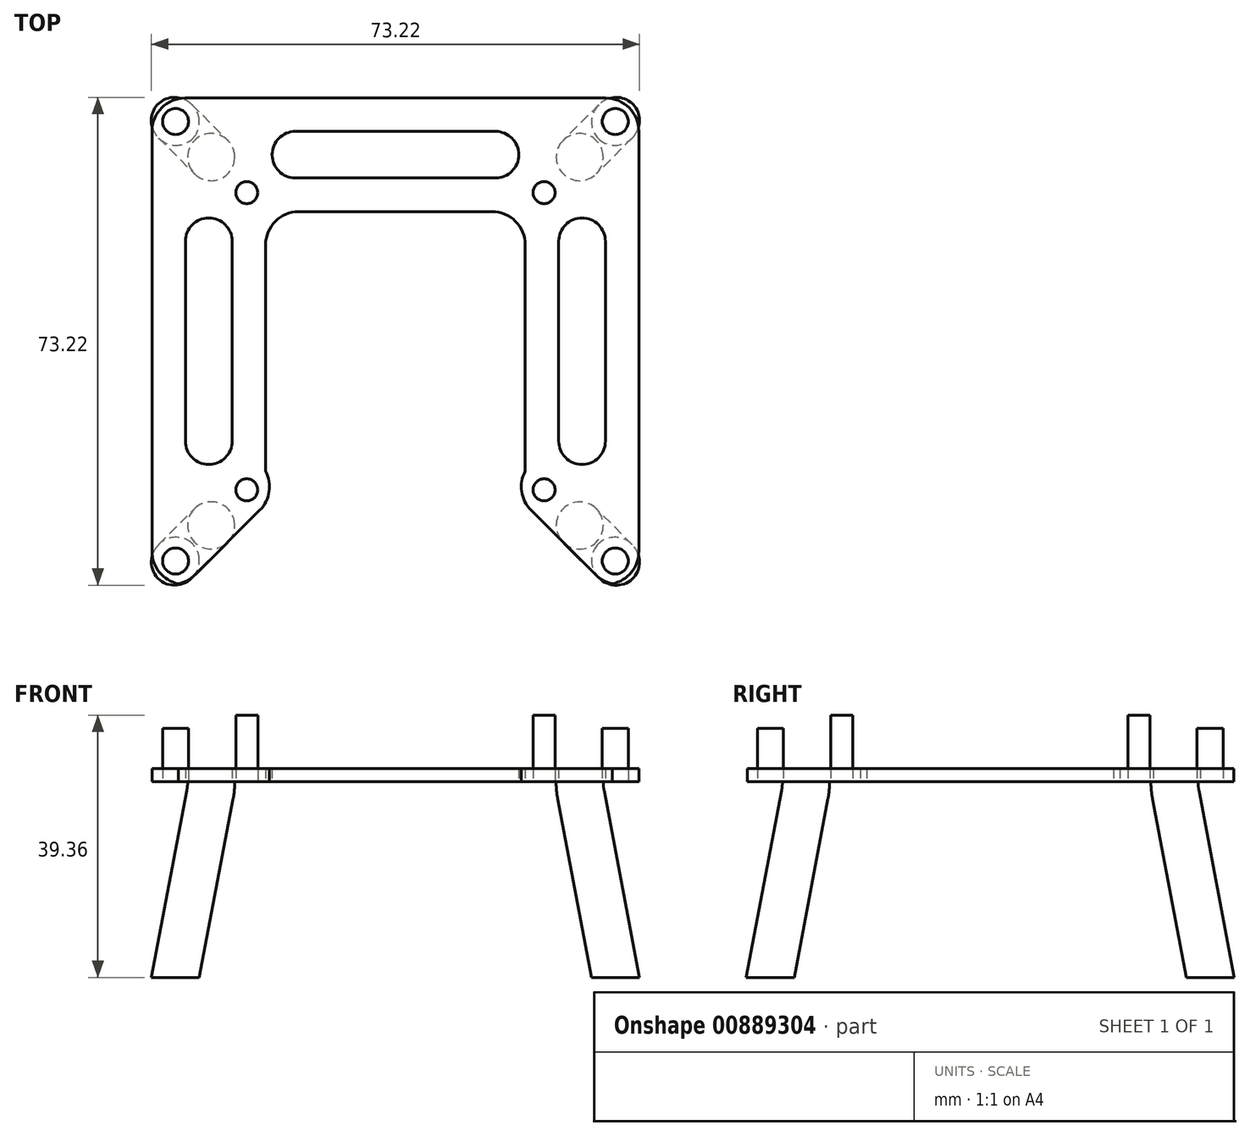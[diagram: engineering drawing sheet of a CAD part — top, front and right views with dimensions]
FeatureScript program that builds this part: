
annotation { "Feature Type Name" : "Feature", "Feature Type Description" : "" }
export const myFeature = defineFeature(function(context is Context, id is Id, definition is map)
    precondition{}
    {
        {
            var Q0;
            Q0=qCreatedBy(makeId("Top.planeOp"),FACE);
            var sketch = newSketch(context, id + "F0", { "sketchPlane" : qUnion([Q0])});
            skLineSegment(sketch, "E0.bottom", {"start": v(22.3, 22.3) * mm, "end": v(-22.3, 22.3) * mm, "construction": true});
            skLineSegment(sketch, "E0.top", {"start": v(22.3, -22.3) * mm, "end": v(-22.3, -22.3) * mm, "construction": true});
            skLineSegment(sketch, "E0.left", {"start": v(22.3, 22.3) * mm, "end": v(22.3, -22.3) * mm, "construction": true});
            skLineSegment(sketch, "E0.right", {"start": v(-22.3, 22.3) * mm, "end": v(-22.3, -22.3) * mm, "construction": true});
            skPoint(sketch, "E0.middle", {"position": v(0, 0) * mm});
            skLineSegment(sketch, "E1", {"start": v(0, 0) * mm, "end": v(-22.3, 22.3) * mm, "construction": true});
            skLineSegment(sketch, "E2", {"start": v(-22.3, 22.3) * mm, "end": v(-41, 41) * mm, "construction": true});
            skCircle(sketch, "E3", {"center": v(-32.98, 32.98) * mm, "radius": 1.95 * mm});
            skCircle(sketch, "E4", {"center": v(-22.3, 22.3) * mm, "radius": 1.65 * mm});
            skCircle(sketch, "E5.1.0", {"center": v(-32.98, -32.98) * mm, "radius": 1.95 * mm});
            skCircle(sketch, "E5.1.1", {"center": v(-22.3, -22.3) * mm, "radius": 1.65 * mm});
            skCircle(sketch, "E5.2.0", {"center": v(32.98, -32.98) * mm, "radius": 1.95 * mm});
            skCircle(sketch, "E5.2.1", {"center": v(22.3, -22.3) * mm, "radius": 1.65 * mm});
            skCircle(sketch, "E5.3.0", {"center": v(32.98, 32.98) * mm, "radius": 1.95 * mm});
            skCircle(sketch, "E5.3.1", {"center": v(22.3, 22.3) * mm, "radius": 1.65 * mm});
            skLineSegment(sketch, "E6", {"start": v(0, 0) * mm, "end": v(22.3, -22.3) * mm, "construction": true});
            skLineSegment(sketch, "E7", {"start": v(0, 0) * mm, "end": v(22.3, 22.3) * mm, "construction": true});
            skLineSegment(sketch, "E8", {"start": v(0, 0) * mm, "end": v(-22.3, -22.3) * mm, "construction": true});
            skLineSegment(sketch, "E9.bottom", {"start": v(32.98, 32.98) * mm, "end": v(-32.98, 32.98) * mm, "construction": true});
            skLineSegment(sketch, "E9.top", {"start": v(32.98, -32.98) * mm, "end": v(-32.98, -32.98) * mm, "construction": true});
            skLineSegment(sketch, "E9.left", {"start": v(32.98, 32.98) * mm, "end": v(32.98, -32.98) * mm, "construction": true});
            skLineSegment(sketch, "E9.right", {"start": v(-32.98, 32.98) * mm, "end": v(-32.98, -32.98) * mm, "construction": true});
            skLineSegment(sketch, "E10.bottom", {"start": v(19.47, 19.47) * mm, "end": v(-19.47, 19.47) * mm});
            skLineSegment(sketch, "E10.top", {"start": v(19.47, -19.47) * mm, "end": v(-14.47, -19.47) * mm});
            skLineSegment(sketch, "E10.left", {"start": v(19.47, 19.47) * mm, "end": v(19.47, -19.47) * mm});
            skLineSegment(sketch, "E10.right", {"start": v(-19.47, 19.47) * mm, "end": v(-19.47, -19.47) * mm});
            skLineSegment(sketch, "E11.bottom", {"start": v(36.51, 36.51) * mm, "end": v(-36.51, 36.51) * mm});
            skLineSegment(sketch, "E11.top", {"start": v(36.51, -36.51) * mm, "end": v(-36.51, -36.51) * mm});
            skLineSegment(sketch, "E11.left", {"start": v(36.51, 36.51) * mm, "end": v(36.51, -36.51) * mm});
            skLineSegment(sketch, "E11.right", {"start": v(-36.51, 36.51) * mm, "end": v(-36.51, -36.51) * mm});
            skLineSegment(sketch, "E12", {"start": v(22.3, 22.3) * mm, "end": v(45.23, 45.23) * mm, "construction": true});
            skLineSegment(sketch, "E13", {"start": v(14.47, -19.47) * mm, "end": v(31.51, -36.51) * mm});
            skLineSegment(sketch, "E14", {"start": v(-14.47, -19.47) * mm, "end": v(-31.51, -36.51) * mm});
            skLineSegment(sketch, "E15", {"start": v(-14.47, -19.47) * mm, "end": v(-19.47, -19.47) * mm});
            skLineSegment(sketch, "E16", {"start": v(-31.51, -36.51) * mm, "end": v(-31.51, -36.51) * mm});
            skLineSegment(sketch, "E17", {"start": v(-36.51, 0) * mm, "end": v(-19.47, 0) * mm, "construction": true});
            skLineSegment(sketch, "E18", {"start": v(-28, 0) * mm, "end": v(-28, 15) * mm, "construction": true});
            skLineSegment(sketch, "E19", {"start": v(-28, 15) * mm, "end": v(-28, -15) * mm, "construction": true});
            skArc(sketch, "E20.0.startCap", {"start": v(-31.5, 15) * mm, "mid": v(-28, 18.5) * mm, "end": v(-24.5, 15) * mm});
            skArc(sketch, "E20.0.endCap", {"start": v(-24.5, -15) * mm, "mid": v(-28, -18.5) * mm, "end": v(-31.5, -15) * mm});
            skLineSegment(sketch, "E20.0.left", {"start": v(-24.5, 15) * mm, "end": v(-24.5, -15) * mm});
            skLineSegment(sketch, "E20.0.right", {"start": v(-31.5, 15) * mm, "end": v(-31.5, -15) * mm});
            skLineSegment(sketch, "E21.1.0", {"start": v(-15, -31.5) * mm, "end": v(15, -31.5) * mm});
            skArc(sketch, "E21.1.1", {"start": v(-15, -31.5) * mm, "mid": v(-18.5, -28) * mm, "end": v(-15, -24.5) * mm});
            skLineSegment(sketch, "E21.1.2", {"start": v(-15, -24.5) * mm, "end": v(15, -24.5) * mm});
            skArc(sketch, "E21.1.3", {"start": v(15, -24.5) * mm, "mid": v(18.5, -28) * mm, "end": v(15, -31.5) * mm});
            skLineSegment(sketch, "E21.2.0", {"start": v(31.5, -15) * mm, "end": v(31.5, 15) * mm});
            skArc(sketch, "E21.2.1", {"start": v(31.5, -15) * mm, "mid": v(28, -18.5) * mm, "end": v(24.5, -15) * mm});
            skLineSegment(sketch, "E21.2.2", {"start": v(24.5, -15) * mm, "end": v(24.5, 15) * mm});
            skArc(sketch, "E21.2.3", {"start": v(24.5, 15) * mm, "mid": v(28, 18.5) * mm, "end": v(31.5, 15) * mm});
            skLineSegment(sketch, "E21.3.0", {"start": v(15, 31.5) * mm, "end": v(-15, 31.5) * mm});
            skArc(sketch, "E21.3.1", {"start": v(15, 31.5) * mm, "mid": v(18.5, 28) * mm, "end": v(15, 24.5) * mm});
            skLineSegment(sketch, "E21.3.2", {"start": v(15, 24.5) * mm, "end": v(-15, 24.5) * mm});
            skArc(sketch, "E21.3.3", {"start": v(-15, 24.5) * mm, "mid": v(-18.5, 28) * mm, "end": v(-15, 31.5) * mm});
            skLineSegment(sketch, "E22", {"start": v(-32.98, -32.98) * mm, "end": v(-22.3, -22.3) * mm, "construction": true});
            skCircle(sketch, "E23", {"center": v(-27.64, -27.64) * mm, "radius": 3.54 * mm});
            skLineSegment(sketch, "E24", {"start": v(-32.98, -32.98) * mm, "end": v(-39.83, -26.12) * mm, "construction": true});
            skCircle(sketch, "E25.1.0", {"center": v(27.64, -27.64) * mm, "radius": 3.54 * mm});
            skLineSegment(sketch, "E25.1.1", {"start": v(32.98, -32.98) * mm, "end": v(26.12, -39.83) * mm, "construction": true});
            skCircle(sketch, "E25.2.0", {"center": v(27.64, 27.64) * mm, "radius": 3.54 * mm});
            skLineSegment(sketch, "E25.2.1", {"start": v(32.98, 32.98) * mm, "end": v(39.83, 26.12) * mm, "construction": true});
            skCircle(sketch, "E25.3.0", {"center": v(-27.64, 27.64) * mm, "radius": 3.54 * mm});
            skLineSegment(sketch, "E25.3.1", {"start": v(-32.98, 32.98) * mm, "end": v(-26.12, 39.83) * mm, "construction": true});
            skSolve(sketch);
        }
        {
            var Q0;
            Q0=makeQuery(id+"F0.imprint","IMPRINT",FACE,{"disambiguationData":[TD([[makeQuery(id+"F0.imprint","IMPRINT",EDGE,{"derivedFrom":sQuery(id+"F0.wireOp",EDGE,"E3")}),-1.0]])]});
            var Q1;
            Q1=makeQuery(id+"F0.imprint","IMPRINT",FACE,{"disambiguationData":[TD([[makeQuery(id+"F0.imprint","IMPRINT",EDGE,{"derivedFrom":sQuery(id+"F0.wireOp",EDGE,"E23")}),1.0]])]});
            var Q2;
            Q2=makeQuery(id+"F0.imprint","IMPRINT",FACE,{"disambiguationData":[TD([[makeQuery(id+"F0.imprint","IMPRINT",EDGE,{"derivedFrom":sQuery(id+"F0.wireOp",EDGE,"E25.3.0")}),1.0]])]});
            var Q3;
            Q3=makeQuery(id+"F0.imprint","IMPRINT",FACE,{"disambiguationData":[TD([[makeQuery(id+"F0.imprint","IMPRINT",EDGE,{"derivedFrom":sQuery(id+"F0.wireOp",EDGE,"E25.1.0")}),1.0]])]});
            var Q4;
            Q4=makeQuery(id+"F0.imprint","IMPRINT",FACE,{"disambiguationData":[TD([[makeQuery(id+"F0.imprint","IMPRINT",EDGE,{"derivedFrom":sQuery(id+"F0.wireOp",EDGE,"E25.2.0")}),1.0]])]});
            extrude(context, id + "F1", {"entities" : qUnion([Q0, Q1, Q2, Q3, Q4]), "depth" : 2 * mm, "offsetDistance" : 25 * mm});
        }
        {
            var Q0;
            Q0=makeQuery(id+"F1.opExtrude","SWEPT_EDGE",EDGE,{"disambiguationData":[OSD([sQuery(id+"F0.wireOp",EDGE,"E10.top"),sQuery(id+"F0.wireOp",EDGE,"E14"),sQuery(id+"F0.wireOp",EDGE,"E15")])]});
            var Q1;
            Q1=makeQuery(id+"F1.opExtrude","SWEPT_EDGE",EDGE,{"disambiguationData":[OSD([sQuery(id+"F0.wireOp",EDGE,"E10.top"),sQuery(id+"F0.wireOp",EDGE,"E13")])]});
            var Q2;
            Q2=makeQuery(id+"F1.opExtrude","SWEPT_EDGE",EDGE,{"disambiguationData":[OSD([sQuery(id+"F0.wireOp",EDGE,"E11.top"),sQuery(id+"F0.wireOp",EDGE,"E14")])]});
            var Q3;
            Q3=makeQuery(id+"F1.opExtrude","SWEPT_EDGE",EDGE,{"disambiguationData":[OSD([sQuery(id+"F0.wireOp",EDGE,"E11.top"),sQuery(id+"F0.wireOp",EDGE,"E11.right")])]});
            var Q4;
            Q4=makeQuery(id+"F1.opExtrude","SWEPT_EDGE",EDGE,{"disambiguationData":[OSD([sQuery(id+"F0.wireOp",EDGE,"E11.top"),sQuery(id+"F0.wireOp",EDGE,"E13")])]});
            var Q5;
            Q5=makeQuery(id+"F1.opExtrude","SWEPT_EDGE",EDGE,{"disambiguationData":[OSD([sQuery(id+"F0.wireOp",EDGE,"E11.top"),sQuery(id+"F0.wireOp",EDGE,"E11.left")])]});
            var Q6;
            Q6=makeQuery(id+"F1.opExtrude","SWEPT_EDGE",EDGE,{"disambiguationData":[OSD([sQuery(id+"F0.wireOp",EDGE,"E11.bottom"),sQuery(id+"F0.wireOp",EDGE,"E11.left")])]});
            var Q7;
            Q7=makeQuery(id+"F1.opExtrude","SWEPT_EDGE",EDGE,{"disambiguationData":[OSD([sQuery(id+"F0.wireOp",EDGE,"E11.bottom"),sQuery(id+"F0.wireOp",EDGE,"E11.right")])]});
            var Q8;
            Q8=makeQuery(id+"F1.opExtrude","SWEPT_EDGE",EDGE,{"disambiguationData":[OSD([sQuery(id+"F0.wireOp",EDGE,"E10.bottom"),sQuery(id+"F0.wireOp",EDGE,"E10.right")])]});
            var Q9;
            Q9=makeQuery(id+"F1.opExtrude","SWEPT_EDGE",EDGE,{"disambiguationData":[OSD([sQuery(id+"F0.wireOp",EDGE,"E10.bottom"),sQuery(id+"F0.wireOp",EDGE,"E10.left")])]});
            fillet(context, id + "F2", {"entities" : qUnion([Q0, Q1, Q2, Q3, Q4, Q5, Q6, Q7, Q8, Q9]), "radius" : 5 * mm, "tangentPropagation" : true, "allowEdgeOverflow" : false});
        }
        {
            var Q0;
            Q0=makeQuery(id+"F0.imprint","IMPRINT",FACE,{"disambiguationData":[TD([[makeQuery(id+"F0.imprint","IMPRINT",EDGE,{"derivedFrom":sQuery(id+"F0.wireOp",EDGE,"E23")}),1.0]])]});
            var Q1;
            Q1=sQuery(id+"F0.wireOp",EDGE,"E24");
            revolve(context, id + "F3", {"operationType" : NewBodyOperationType.ADD, "surfaceOperationType" : NewSurfaceOperationType.NEW, "entities" : qUnion([Q0]), "axis" : qUnion([Q1]), "revolveType" : RevolveType.ONE_DIRECTION, "angle" : 15 * degree});
        }
        {
            var Q0;
            Q0=makeQuery(id+"F3.opRevolve","CAP_FACE",FACE,{"disambiguationData":[OSD([sQuery(id+"F0.wireOp",EDGE,"E23")])],"isStart":false});
            extrude(context, id + "F4", {"entities" : qUnion([Q0]), "operationType" : NewBodyOperationType.ADD, "depth" : 30 * mm, "offsetDistance" : 25 * mm});
        }
        {
            var Q0;
            Q0=makeQuery(id+"F0.imprint","IMPRINT",FACE,{"disambiguationData":[TD([[makeQuery(id+"F0.imprint","IMPRINT",EDGE,{"derivedFrom":sQuery(id+"F0.wireOp",EDGE,"E25.3.0")}),1.0]])]});
            var Q1;
            Q1=sQuery(id+"F0.wireOp",EDGE,"E25.3.1");
            revolve(context, id + "F5", {"operationType" : NewBodyOperationType.ADD, "surfaceOperationType" : NewSurfaceOperationType.NEW, "entities" : qUnion([Q0]), "axis" : qUnion([Q1]), "revolveType" : RevolveType.ONE_DIRECTION, "angle" : 15 * degree});
        }
        {
            var Q0;
            Q0=makeQuery(id+"F0.imprint","IMPRINT",FACE,{"disambiguationData":[TD([[makeQuery(id+"F0.imprint","IMPRINT",EDGE,{"derivedFrom":sQuery(id+"F0.wireOp",EDGE,"E25.2.0")}),1.0]])]});
            var Q1;
            Q1=sQuery(id+"F0.wireOp",EDGE,"E25.2.1");
            revolve(context, id + "F6", {"operationType" : NewBodyOperationType.ADD, "surfaceOperationType" : NewSurfaceOperationType.NEW, "entities" : qUnion([Q0]), "axis" : qUnion([Q1]), "revolveType" : RevolveType.ONE_DIRECTION, "angle" : 15 * degree});
        }
        {
            var Q0;
            Q0=makeQuery(id+"F0.imprint","IMPRINT",FACE,{"disambiguationData":[TD([[makeQuery(id+"F0.imprint","IMPRINT",EDGE,{"derivedFrom":sQuery(id+"F0.wireOp",EDGE,"E25.1.0")}),1.0]])]});
            var Q1;
            Q1=sQuery(id+"F0.wireOp",EDGE,"E25.1.1");
            revolve(context, id + "F7", {"operationType" : NewBodyOperationType.ADD, "surfaceOperationType" : NewSurfaceOperationType.NEW, "entities" : qUnion([Q0]), "axis" : qUnion([Q1]), "revolveType" : RevolveType.ONE_DIRECTION, "angle" : 15 * degree});
        }
        {
            var Q0;
            Q0=makeQuery(id+"F5.opRevolve","CAP_FACE",FACE,{"disambiguationData":[OSD([sQuery(id+"F0.wireOp",EDGE,"E25.3.0")])],"isStart":false});
            extrude(context, id + "F8", {"entities" : qUnion([Q0]), "operationType" : NewBodyOperationType.ADD, "depth" : 30 * mm, "offsetDistance" : 25 * mm});
        }
        {
            var Q0;
            Q0=makeQuery(id+"F6.opRevolve","CAP_FACE",FACE,{"disambiguationData":[OSD([sQuery(id+"F0.wireOp",EDGE,"E25.2.0")])],"isStart":false});
            extrude(context, id + "F9", {"entities" : qUnion([Q0]), "operationType" : NewBodyOperationType.ADD, "depth" : 30 * mm, "offsetDistance" : 25 * mm});
        }
        {
            var Q0;
            Q0=makeQuery(id+"F7.opRevolve","CAP_FACE",FACE,{"disambiguationData":[OSD([sQuery(id+"F0.wireOp",EDGE,"E25.1.0")])],"isStart":false});
            extrude(context, id + "F10", {"entities" : qUnion([Q0]), "operationType" : NewBodyOperationType.ADD, "depth" : 30 * mm, "offsetDistance" : 25 * mm});
        }
        {
            var Q0;
            Q0=qCreatedBy(makeId("Right.planeOp"),FACE);
            var sketch = newSketch(context, id + "F11", { "sketchPlane" : qUnion([Q0])});
            skLineSegment(sketch, "E26.bottom", {"start": v(45.85, -29.36) * mm, "end": v(-45.85, -29.36) * mm});
            skLineSegment(sketch, "E26.top", {"start": v(45.85, -33.74) * mm, "end": v(-45.85, -33.74) * mm});
            skLineSegment(sketch, "E26.left", {"start": v(45.85, -29.36) * mm, "end": v(45.85, -33.74) * mm});
            skLineSegment(sketch, "E26.right", {"start": v(-45.85, -29.36) * mm, "end": v(-45.85, -33.74) * mm});
            skPoint(sketch, "E26.middle", {"position": v(0, -31.55) * mm});
            skSolve(sketch);
        }
        {
            var Q0;
            Q0=makeQuery(id+"F11.imprint","IMPRINT",FACE,{"disambiguationData":[TD([[makeQuery(id+"F11.imprint","IMPRINT",EDGE,{"derivedFrom":sQuery(id+"F11.wireOp",EDGE,"E26.bottom")}),1.0]])]});
            extrude(context, id + "F12", {"entities" : qUnion([Q0]), "operationType" : NewBodyOperationType.REMOVE, "oppositeDirection" : true, "depth" : 40 * mm, "offsetDistance" : 25 * mm, "hasSecondDirection" : true, "secondDirectionOppositeDirection" : false, "secondDirectionDepth" : 40 * mm});
        }
        {
            var Q0;
            Q0=makeQuery(id+"F0.imprint","IMPRINT",FACE,{"disambiguationData":[TD([[makeQuery(id+"F0.imprint","IMPRINT",EDGE,{"derivedFrom":sQuery(id+"F0.wireOp",EDGE,"E5.2.1")}),1.0]])]});
            var Q1;
            Q1=makeQuery(id+"F0.imprint","IMPRINT",FACE,{"disambiguationData":[TD([[makeQuery(id+"F0.imprint","IMPRINT",EDGE,{"derivedFrom":sQuery(id+"F0.wireOp",EDGE,"E5.1.1")}),1.0]])]});
            var Q2;
            Q2=makeQuery(id+"F0.imprint","IMPRINT",FACE,{"disambiguationData":[TD([[makeQuery(id+"F0.imprint","IMPRINT",EDGE,{"derivedFrom":sQuery(id+"F0.wireOp",EDGE,"E4")}),1.0]])]});
            var Q3;
            Q3=makeQuery(id+"F0.imprint","IMPRINT",FACE,{"disambiguationData":[TD([[makeQuery(id+"F0.imprint","IMPRINT",EDGE,{"derivedFrom":sQuery(id+"F0.wireOp",EDGE,"E5.3.1")}),1.0]])]});
            extrude(context, id + "F13", {"entities" : qUnion([Q0, Q1, Q2, Q3]), "depth" : 10 * mm, "offsetDistance" : 25 * mm});
        }
        {
            var Q0;
            Q0=makeQuery(id+"F0.imprint","IMPRINT",FACE,{"disambiguationData":[TD([[makeQuery(id+"F0.imprint","IMPRINT",EDGE,{"derivedFrom":sQuery(id+"F0.wireOp",EDGE,"E5.2.0")}),1.0]])]});
            var Q1;
            Q1=makeQuery(id+"F0.imprint","IMPRINT",FACE,{"disambiguationData":[TD([[makeQuery(id+"F0.imprint","IMPRINT",EDGE,{"derivedFrom":sQuery(id+"F0.wireOp",EDGE,"E5.3.0")}),1.0]])]});
            var Q2;
            Q2=makeQuery(id+"F0.imprint","IMPRINT",FACE,{"disambiguationData":[TD([[makeQuery(id+"F0.imprint","IMPRINT",EDGE,{"derivedFrom":sQuery(id+"F0.wireOp",EDGE,"E3")}),1.0]])]});
            var Q3;
            Q3=makeQuery(id+"F0.imprint","IMPRINT",FACE,{"disambiguationData":[TD([[makeQuery(id+"F0.imprint","IMPRINT",EDGE,{"derivedFrom":sQuery(id+"F0.wireOp",EDGE,"E5.1.0")}),1.0]])]});
            extrude(context, id + "F14", {"entities" : qUnion([Q0, Q1, Q2, Q3]), "depth" : 8 * mm, "offsetDistance" : 25 * mm});
        }
    });
